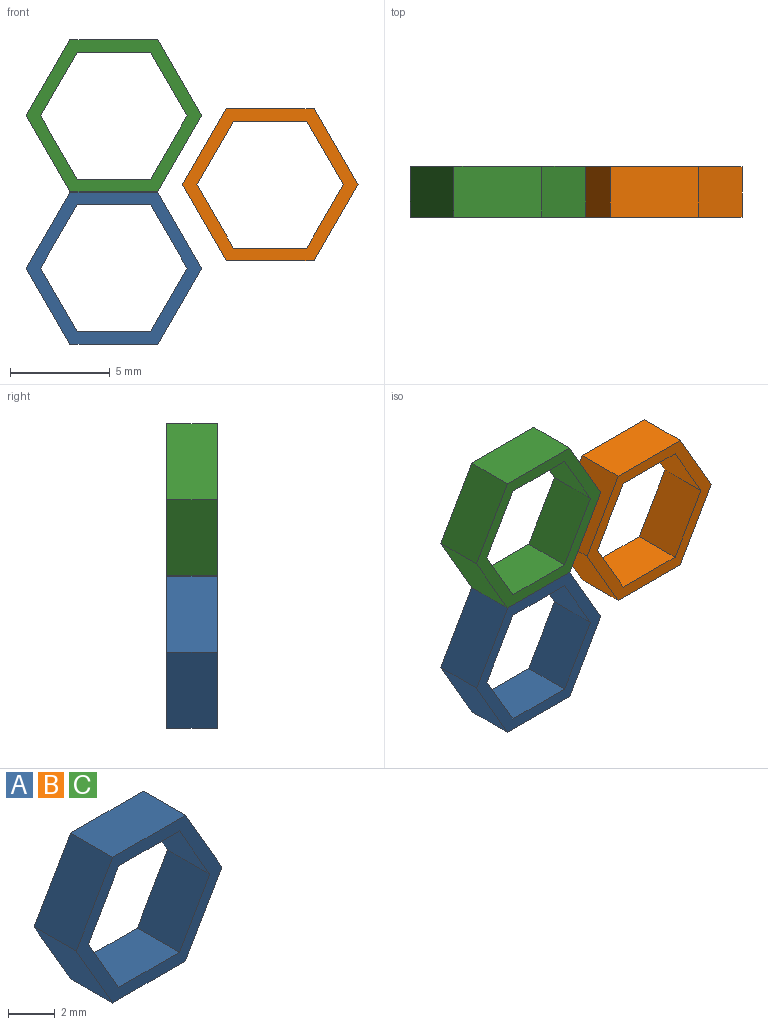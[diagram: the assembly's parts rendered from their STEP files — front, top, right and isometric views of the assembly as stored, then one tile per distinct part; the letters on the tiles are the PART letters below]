
ASSEMBLY  parts=3 mates=3
PART A: 14 faces, bbox 8.8x2.5x7.6 mm
  f0: plane 3.18x2.54mm, normal (0.87,0,0.5), area 9.3mm2, adj f1,f11,f12,f13
  f1: plane 3.18x2.54mm, normal (0.87,0,-0.5), area 9.3mm2, adj f0,f2,f12,f13
  f2: plane 3.67x2.54mm, normal (0,0,-1), area 9.3mm2, adj f1,f3,f12,f13
  f3: plane 3.18x2.54mm, normal (-0.87,0,-0.5), area 9.3mm2, adj f2,f4,f12,f13
  f4: plane 3.18x2.54mm, normal (-0.87,0,0.5), area 9.3mm2, adj f3,f11,f12,f13
  f5: plane 3.81x2.54mm, normal (-0.87,0,0.5), area 11.2mm2, adj f6,f10,f12,f13
  f6: plane 3.81x2.54mm, normal (-0.87,0,-0.5), area 11.2mm2, adj f5,f7,f12,f13
  f7: plane 4.4x2.54mm, normal (0,0,-1), area 11.2mm2, adj f6,f8,f12,f13
  f8: plane 3.81x2.54mm, normal (0.87,0,-0.5), area 11.2mm2, adj f7,f9,f12,f13
  f9: plane 3.81x2.54mm, normal (0.87,0,0.5), area 11.2mm2, adj f8,f10,f12,f13
  f10: plane 4.4x2.54mm, normal (0,0,1), area 11.2mm2, adj f5,f9,f12,f13
  f11: plane 3.67x2.54mm, normal (0,0,1), area 9.3mm2, adj f0,f4,f12,f13
  f12: plane 8.8x7.62mm, normal (0,-1,0), area 15.4mm2, adj f0,f1,f2,f3,f4,f5,f6,f7
  f13: plane 8.8x7.62mm, normal (0,1,0), area 15.4mm2, adj f0,f1,f2,f3,f4,f5,f6,f7
PART B: same geometry as A
PART C: same geometry as A
PLACE A t=(-3.3,0,-1.91)mm
PLACE B t=(4.53,0,2.27)mm
PLACE C t=(-3.3,0,5.72)mm
MATE planar B.f13 <-> C.f13  axis (0,1,0) through (1.78,0,3.86)mm
MATE planar B.f13 <-> C.f13  axis (0,1,0) through (4.53,0,2.27)mm
MATE fastened A.f10 <-> C.f7  axis (0,0,1) through (-3.3,-1.27,1.91)mm
